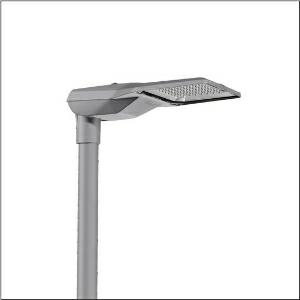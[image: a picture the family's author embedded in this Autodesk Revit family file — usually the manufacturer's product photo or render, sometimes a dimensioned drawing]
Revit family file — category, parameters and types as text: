
# Revit family: streetlight_sl_21_iq_midi___p0_8ab_5xe3r31v08nb_094b
name_source: partatom
category: Lighting Fixtures
units: mm (PartAtom-declared; Revit-internal decimal feet)

## family parameters
Cut with Voids When Loaded = No
Host = Face
Light Source = No
Part Type = Normal
Room Calculation Point = No
Round Connector Dimension = Use Diameter
Shared = No

## types (1)
- --- (1 x LED, 18710 lm, 136.6 W, 3000K)
    Apparent Load = 137 VA
    CIE Flux Codes = 39 72 97 100 100
    Color Rendering = 70
    Color Temperature = 3000K
    Default Elevation = 1800 mm
    Description = Streetlight SL 21 iQ midi, mast luminaire, primary light control with lens, of PMMA, primary optical cover: cover, of toughened safety glass, transparent, light distribution: P0.8aB, light emission: direct distribution, primary light characteristic: asymmetric, installation type: post-top, side-entry, LED, High Power LED, rated luminous flux: 18.710lm, luminous efficacy: 137lm/W, light colour: 730, colour temperature: 3000K, control gear: iQ-Street Remote, D4i with power reduction, control: pre-setting: logarithmic dimming characteristic, Street-Remote, Auto-Match, Temp-Guard, Lumen-Switch, Night-Set, Smart-Wire, Light-Fading, Desk-Remote (wireless, voltage-free reading and setting of iQ features in the workshop via application-optimized NFC function/RFID function), optimised constant luminous flux control (CLO 2.0), mains connection: 230..240V, AC, 50/60Hz, start of lifetime: 137W, end of service life: 144W, reduction: 61W, luminaire housing, of diecast aluminium, powder-coated, Siteco® metallic grey (DB 702S), corrosivity category C5 mid according to DIN EN ISO 12944, please order mast flange separately, inclination adjustable: 0°, 5°, 10°, 15°, sealing non-destructively replaceable, multi-level sealing system, length: 644mm, width: 335mm, height: 110mm, mast flange for spigot size: 42mm (side-entry): 5XC10008XM4, 60/48mm (side-entry/post-top): 5XC10108XM2, 76/60mm (side-entry/post-top): 5XC10108XM1, mounting height: 4..8m, Smart Interface above, protection rating (complete): IP66, insulation class (complete): insulation class II (safety insulation), certification: CE, ENEC, ENEC+, VDE, impact resistance: IK09, permissible operating ambient temperature for outdoor applications: -40..+50°C, standard-compliant lighting for roads and squares, packaging unit: 1 piece

Light Distribution: P0.8aB
    Height = 111 mm
    Lamp = 1 x LED
    Lamp Light Flux = 18710 lm
    Lamp Power = 136.6 W
    Lamp count = 1
    Length = 644 mm
    Luminous efficacy = 137 lm/W
    Manufacturer = Siteco
    ModVariant = No
    Model = 5XE3R31V08NB
    Number of Poles = 1
    OnlyDefault = Yes
    Power Factor = 1
    Product Name = Streetlight SL 21 iQ midi | P0.8aB
    Product group = mast luminaire | pylon top
    ProductGroupID = 6100
    Protection Class = Protection class II
    Protection Degree = IP 66
    RLX_Detail_Level = 1
    RLX_Emergency_Light_Flux = 0 lm
    RLX_Emergency_Type = 0
    RLX_Emergency_Type_DB = No
    RlxData = <blob elided: 90921 chars, md5=251f33b7>
    Socket = socket
    Standby Power = 0 W
    System Light Flux = 18710 lm
    System Power = 137 W
    Type Comments = factory setting: luminous flux: 100 % | dim-lin: 254 | 733 mA
    Type Image = l_1004302.jpg
    URL = http://relux.com
    VarID = @adj_068180
    Voltage = 0 V
    Weight = 0.00 kg
    Width = 336 mm

## geometry (parser evidence)
native form markers: Blend x4, Sweep x11
no freeform markers — native parametric forms only
